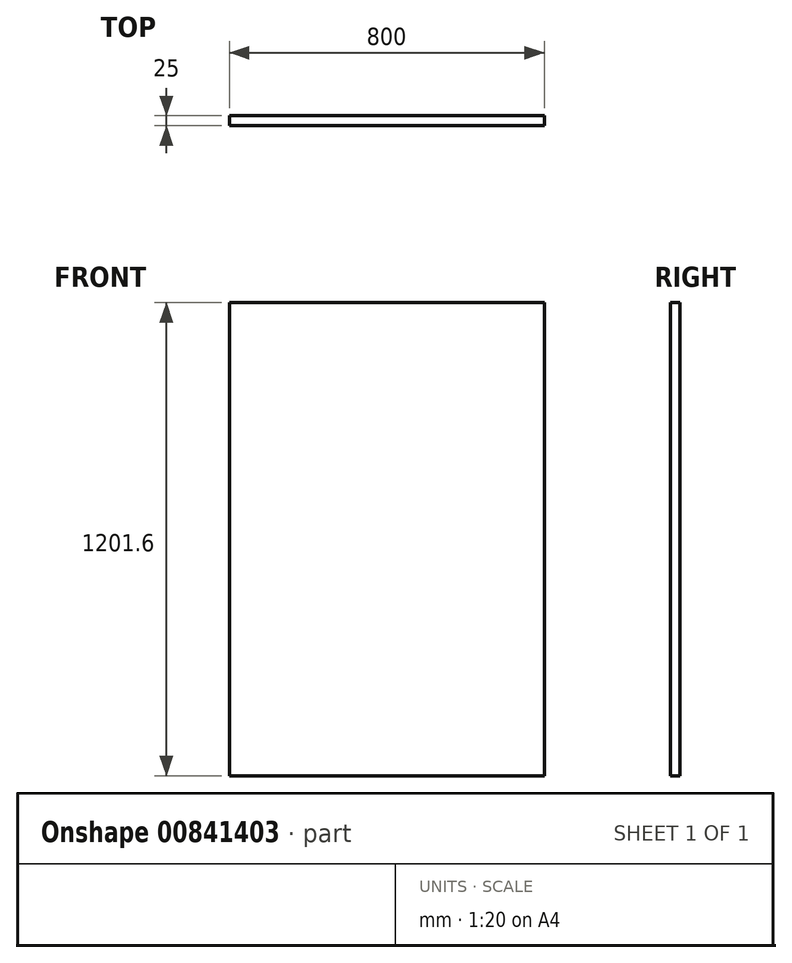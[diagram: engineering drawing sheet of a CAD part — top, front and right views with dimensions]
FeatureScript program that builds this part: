
annotation { "Feature Type Name" : "Feature", "Feature Type Description" : "" }
export const myFeature = defineFeature(function(context is Context, id is Id, definition is map)
    precondition{}
    {
        {
            var Q0;
            Q0=qCreatedBy(makeId("Front.planeOp"),FACE);
            var sketch = newSketch(context, id + "F0", { "sketchPlane" : qUnion([Q0])});
            skLineSegment(sketch, "E0.bottom", {"start": v(400, 600.8) * mm, "end": v(-400, 600.8) * mm});
            skLineSegment(sketch, "E0.top", {"start": v(400, -600.8) * mm, "end": v(-400, -600.8) * mm});
            skLineSegment(sketch, "E0.left", {"start": v(400, 600.8) * mm, "end": v(400, -600.8) * mm});
            skLineSegment(sketch, "E0.right", {"start": v(-400, 600.8) * mm, "end": v(-400, -600.8) * mm});
            skPoint(sketch, "E0.middle", {"position": v(0, 0) * mm});
            skSolve(sketch);
        }
        {
            var Q0;
            Q0 = qSketchRegion(id + "F0", true);
            extrude(context, id + "F1", {"entities" : qUnion([Q0]), "depth" : 25 * mm, "offsetDistance" : 25 * mm});
        }
    });
